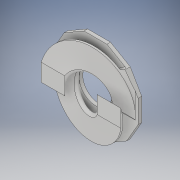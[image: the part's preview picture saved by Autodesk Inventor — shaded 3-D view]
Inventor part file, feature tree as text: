
AUTODESK INVENTOR PART (.ipt)
format: ipt  version: 2018 (Build 220112000, 112)  size: 377,344 bytes
history: native  units: in
note: dims shown in document units (in); Inventor stores cm internally (conversion verified against a paired STEP export)
features: fillet x2, extrude x1, helix x1, sketch x1
ambient origin geometry x8: Origin, YZ Plane, XZ Plane, XY Plane, X Axis, Y Axis, Z Axis, Center Point
bodies: Solid1 (feature_tree)
feature tree (5):
  extrude  "Extrusion1"  Depth=0.125in TaperAngle=0.0deg
  helix  "Coil1"  [1 undecoded]
  fillet  "Fillet1"  Radius=0.3in
  fillet  "Fillet2"  Radius=0.3in
  sketch  "Sketch2"  dims[d0=1.125in d2=0.125in d3=0.0in d4=2.95in d5=0.3in d6=0.3in d7=0.3in d8=0.3in d9=1.0in d10=0.5in d11=0.1969in d12=0.0in d13=90.0deg d14=90.0deg d15=0.0in d16=0.0in d17=0.125in d18=0.05in d19=0.1in d20=0.1in]
note: 1 required parameter value undecoded (feature->parameter linkage not recoverable at this tier; creation-order binding heuristic only, values carry confidence <= 0.55)
